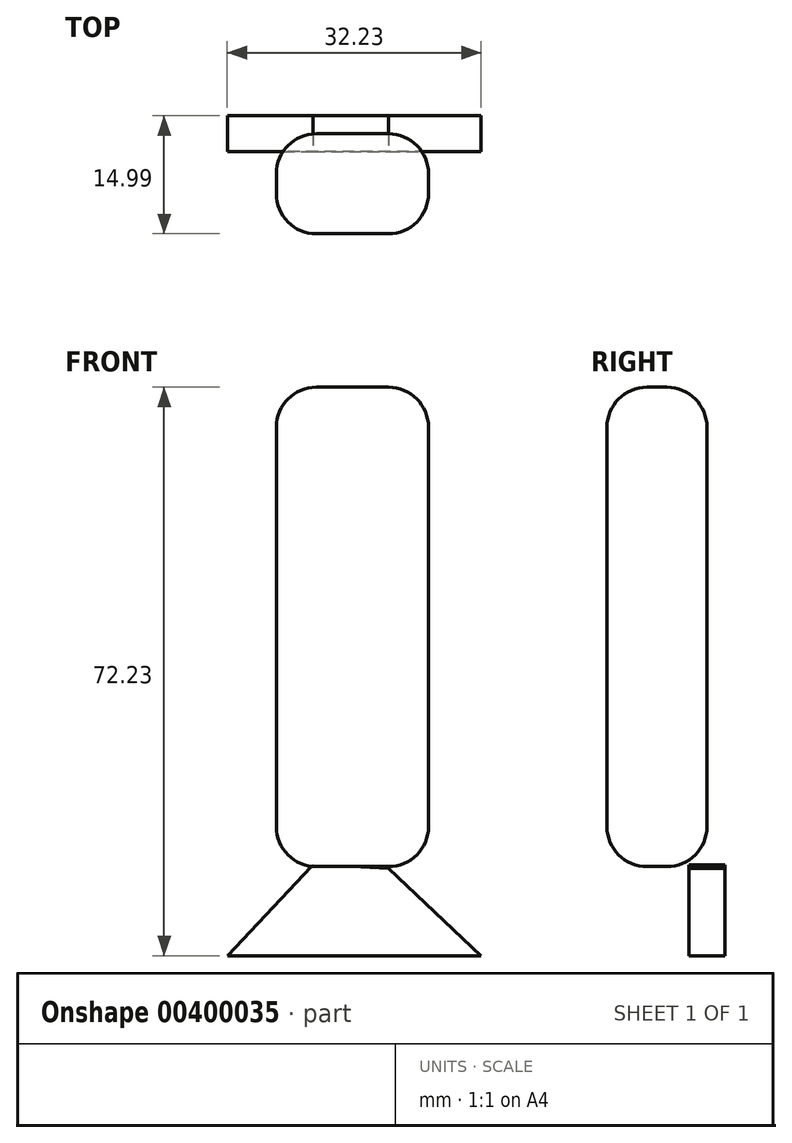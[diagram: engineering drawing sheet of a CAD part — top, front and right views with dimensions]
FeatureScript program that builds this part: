
annotation { "Feature Type Name" : "Feature", "Feature Type Description" : "" }
export const myFeature = defineFeature(function(context is Context, id is Id, definition is map)
    precondition{}
    {
        {
            var Q0;
            Q0=qCreatedBy(makeId("Front.planeOp"),FACE);
            var sketch = newSketch(context, id + "F0", { "sketchPlane" : qUnion([Q0])});
            skLineSegment(sketch, "E0", {"start": v(-9.11, 55.12) * mm, "end": v(-9.11, -5.78) * mm});
            skLineSegment(sketch, "E1", {"start": v(-9.11, -5.78) * mm, "end": v(10.22, -5.78) * mm});
            skLineSegment(sketch, "E2", {"start": v(10.22, -5.78) * mm, "end": v(10.22, 55.12) * mm});
            skLineSegment(sketch, "E3", {"start": v(10.22, 55.12) * mm, "end": v(-9.11, 55.12) * mm});
            skSolve(sketch);
        }
        {
            var Q0;
            Q0=makeQuery(id+"F0.imprint","IMPRINT",FACE,{"disambiguationData":[TD([[makeQuery(id+"F0.imprint","IMPRINT",EDGE,{"derivedFrom":sQuery(id+"F0.wireOp",EDGE,"E0")}),1.0]])]});
            extrude(context, id + "F1", {"entities" : qUnion([Q0]), "depth" : 12.7 * mm});
        }
        {
            var Q0;
            Q0=makeQuery(id+"F1.opExtrude","SWEPT_FACE",FACE,{"disambiguationData":[OSD([sQuery(id+"F0.wireOp",EDGE,"E0")])]});
            var Q1;
            Q1=makeQuery(id+"F1.opExtrude","SWEPT_FACE",FACE,{"disambiguationData":[OSD([sQuery(id+"F0.wireOp",EDGE,"E2")])]});
            var Q2;
            Q2=makeQuery(id+"F1.opExtrude","SWEPT_FACE",FACE,{"disambiguationData":[OSD([sQuery(id+"F0.wireOp",EDGE,"E1")])]});
            var Q3;
            Q3=makeQuery(id+"F1.opExtrude","SWEPT_FACE",FACE,{"disambiguationData":[OSD([sQuery(id+"F0.wireOp",EDGE,"E3")])]});
            fillet(context, id + "F2", {"entities" : qUnion([Q0, Q1, Q2, Q3]), "radius" : 5.08 * mm, "tangentPropagation" : true, "allowEdgeOverflow" : false});
        }
        {
            var Q0;
            Q0=qCreatedBy(makeId("Front.planeOp"),FACE);
            var sketch = newSketch(context, id + "F3", { "sketchPlane" : qUnion([Q0])});
            skLineSegment(sketch, "E4", {"start": v(5.11, -6) * mm, "end": v(16.9, -17.11) * mm});
            skLineSegment(sketch, "E5", {"start": v(16.9, -17.11) * mm, "end": v(-15.34, -17.11) * mm});
            skLineSegment(sketch, "E6", {"start": v(-15.34, -17.11) * mm, "end": v(-4.43, -5.55) * mm});
            skLineSegment(sketch, "E7", {"start": v(-4.43, -5.55) * mm, "end": v(5.11, -6) * mm});
            skSolve(sketch);
        }
        {
            var Q0;
            Q0=makeQuery(id+"F3.imprint","IMPRINT",FACE,{"disambiguationData":[TD([[makeQuery(id+"F3.imprint","IMPRINT",EDGE,{"derivedFrom":sQuery(id+"F3.wireOp",EDGE,"E4")}),-1.0]])]});
            extrude(context, id + "F4", {"entities" : qUnion([Q0]), "endBound" : BoundingType.SYMMETRIC, "oppositeDirection" : true, "depth" : 4.57 * mm});
        }
    });
